# Revit family: Haworth_Openest_SprigTable_Round_EU_PRELIMINARY
name_source: partatom
category: Furniture
revit_build: Autodesk Revit 2018 (Build: 20170223_1515(x64)
units: mm (PartAtom-declared; Revit-internal decimal feet)

## family parameters
Always vertical = Yes
Cut with Voids When Loaded = No
OmniClass Number = 23.40.20.00
OmniClass Title = General Furniture and Specialties
Room Calculation Point = No
Shared = No
Work Plane-Based = No

## types (2) — shared parameters
Assembly Code = E2020200
Description = Haworth - Openest - Sprig Table - Round
Manufacturer = Haworth
Model = SODX - XXXX
Revision No. = 1
Size = Verify Final Dim. w/ Haworth
Sustainability Info = https://www.haworth.com
URL = https://www.haworth.com
URL - Product = https://www.haworth.com
Warranty = http://www.haworth.com

## per-type parameters (varying)
| type | Height | Large | Leg Height | Leg Width | Radius | Small |
| Small Table | 43 cm | No | 40 cm | 17 cm | 21 cm | Yes |
| Large Table | 36 cm | Yes | 33 cm | 26 cm | 31 cm | No |

## geometry (parser evidence)
native form markers: Blend x4, Sweep x5
no freeform markers — native parametric forms only
